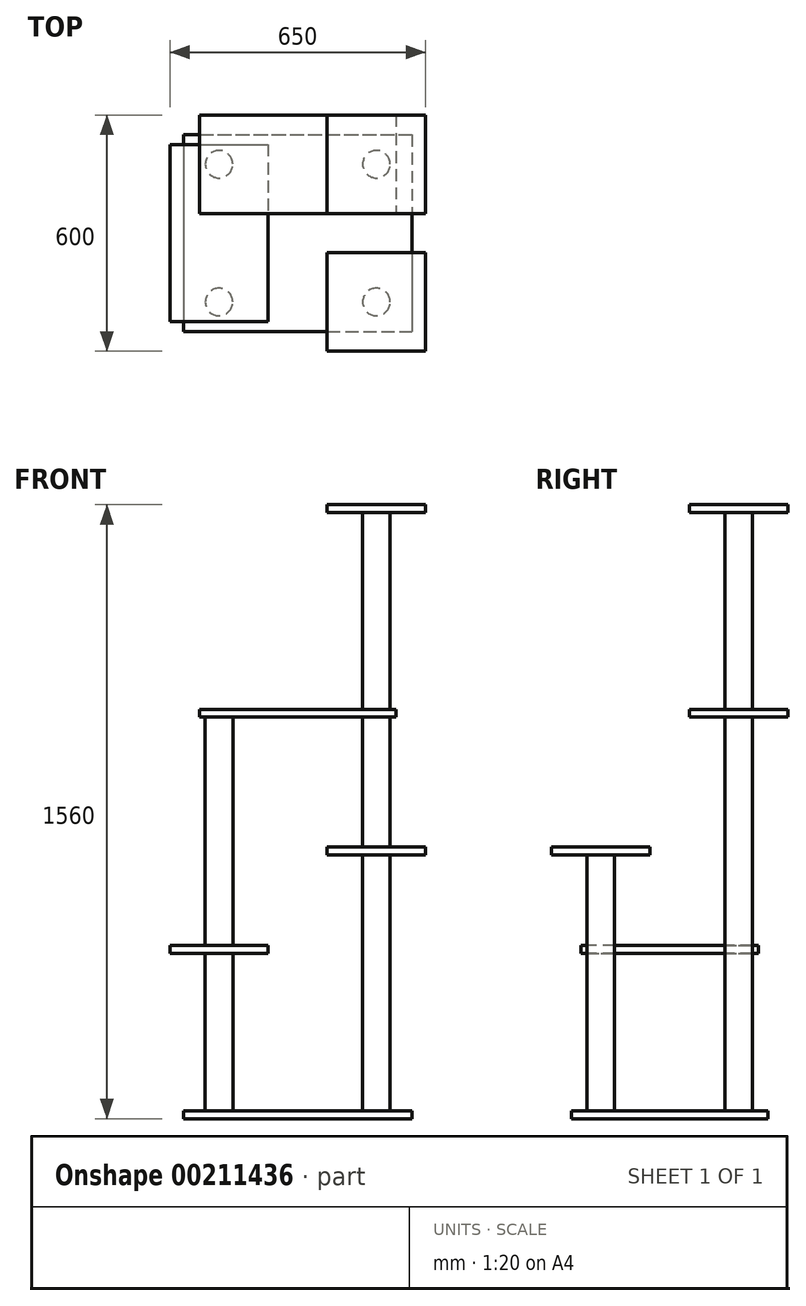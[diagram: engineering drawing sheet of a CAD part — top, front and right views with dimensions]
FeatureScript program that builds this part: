
annotation { "Feature Type Name" : "Feature", "Feature Type Description" : "" }
export const myFeature = defineFeature(function(context is Context, id is Id, definition is map)
    precondition{}
    {
        {
            var Q0;
            Q0=qCreatedBy(makeId("Top.planeOp"),FACE);
            var sketch = newSketch(context, id + "F0", { "sketchPlane" : qUnion([Q0])});
            skLineSegment(sketch, "E0.bottom", {"start": v(-290, 250) * mm, "end": v(290, 250) * mm});
            skLineSegment(sketch, "E0.top", {"start": v(-290, -250) * mm, "end": v(290, -250) * mm});
            skLineSegment(sketch, "E0.left", {"start": v(-290, 250) * mm, "end": v(-290, -250) * mm});
            skLineSegment(sketch, "E0.right", {"start": v(290, 250) * mm, "end": v(290, -250) * mm});
            skPoint(sketch, "E0.middle", {"position": v(0, 0) * mm});
            skSolve(sketch);
        }
        {
            var Q0;
            Q0 = qSketchRegion(id + "F0", true);
            extrude(context, id + "F1", {"entities" : qUnion([Q0]), "depth" : 20 * mm});
        }
        {
            var Q0;
            Q0=makeQuery(id+"F1.opExtrude","CAP_FACE",FACE,{"disambiguationData":[OSD([sQuery(id+"F0.wireOp",EDGE,"E0.bottom"),sQuery(id+"F0.wireOp",EDGE,"E0.top"),sQuery(id+"F0.wireOp",EDGE,"E0.left"),sQuery(id+"F0.wireOp",EDGE,"E0.right")])],"isStart":false});
            var sketch = newSketch(context, id + "F2", { "sketchPlane" : qUnion([Q0])});
            skLineSegment(sketch, "E1.bottom", {"start": v(-200, 175) * mm, "end": v(200, 175) * mm, "construction": true});
            skLineSegment(sketch, "E1.top", {"start": v(-200, -175) * mm, "end": v(200, -175) * mm, "construction": true});
            skLineSegment(sketch, "E1.left", {"start": v(-200, 175) * mm, "end": v(-200, -175) * mm, "construction": true});
            skLineSegment(sketch, "E1.right", {"start": v(200, 175) * mm, "end": v(200, -175) * mm, "construction": true});
            skPoint(sketch, "E1.middle", {"position": v(0, 0) * mm});
            skCircle(sketch, "E2", {"center": v(-200, 175) * mm, "radius": 35 * mm});
            skCircle(sketch, "E3", {"center": v(200, 175) * mm, "radius": 35 * mm});
            skCircle(sketch, "E4", {"center": v(-200, -175) * mm, "radius": 35 * mm});
            skCircle(sketch, "E5", {"center": v(200, -175) * mm, "radius": 35 * mm});
            skSolve(sketch);
        }
        {
            var Q0;
            Q0=makeQuery(id+"F2.imprint","IMPRINT",FACE,{"disambiguationData":[TD([[makeQuery(id+"F2.imprint","IMPRINT",EDGE,{"derivedFrom":sQuery(id+"F2.wireOp",EDGE,"E2")}),1.0]])]});
            var Q1;
            Q1=makeQuery(id+"F2.imprint","IMPRINT",FACE,{"disambiguationData":[TD([[makeQuery(id+"F2.imprint","IMPRINT",EDGE,{"derivedFrom":sQuery(id+"F2.wireOp",EDGE,"E4")}),1.0]])]});
            extrude(context, id + "F3", {"entities" : qUnion([Q0, Q1]), "operationType" : NewBodyOperationType.ADD, "depth" : 400 * mm});
        }
        {
            var Q0;
            Q0=makeQuery(id+"F3.opExtrude","CAP_FACE",FACE,{"disambiguationData":[OSD([sQuery(id+"F2.wireOp",EDGE,"E2")])],"isStart":false});
            var sketch = newSketch(context, id + "F4", { "sketchPlane" : qUnion([Q0])});
            skLineSegment(sketch, "E6.bottom", {"start": v(-325, 225) * mm, "end": v(-75, 225) * mm});
            skLineSegment(sketch, "E6.top", {"start": v(-325, -225) * mm, "end": v(-75, -225) * mm});
            skLineSegment(sketch, "E6.left", {"start": v(-325, 225) * mm, "end": v(-325, -225) * mm});
            skLineSegment(sketch, "E6.right", {"start": v(-75, 225) * mm, "end": v(-75, -225) * mm});
            skPoint(sketch, "E6.middle", {"position": v(-200, 0) * mm});
            skLineSegment(sketch, "E7", {"start": v(-200, 175) * mm, "end": v(-200, -175) * mm, "construction": true});
            skSolve(sketch);
        }
        {
            var Q0;
            Q0 = qSketchRegion(id + "F4", true);
            extrude(context, id + "F5", {"entities" : qUnion([Q0]), "operationType" : NewBodyOperationType.ADD, "depth" : 20 * mm});
        }
        {
            var Q0;
            Q0=makeQuery(id+"F2.imprint","IMPRINT",FACE,{"disambiguationData":[TD([[makeQuery(id+"F2.imprint","IMPRINT",EDGE,{"derivedFrom":sQuery(id+"F2.wireOp",EDGE,"E3")}),1.0]])]});
            extrude(context, id + "F6", {"entities" : qUnion([Q0]), "operationType" : NewBodyOperationType.ADD, "depth" : 1000 * mm});
        }
        {
            var Q0;
            Q0=makeQuery(id+"F5.opExtrude","CAP_FACE",FACE,{"disambiguationData":[OSD([sQuery(id+"F4.wireOp",EDGE,"E6.bottom"),sQuery(id+"F4.wireOp",EDGE,"E6.top"),sQuery(id+"F4.wireOp",EDGE,"E6.left"),sQuery(id+"F4.wireOp",EDGE,"E6.right")])],"isStart":false});
            var sketch = newSketch(context, id + "F7", { "sketchPlane" : qUnion([Q0])});
            skCircle(sketch, "E8.0", {"center": v(-200, 175) * mm, "radius": 35 * mm});
            skSolve(sketch);
        }
        {
            var Q0;
            Q0=makeQuery(id+"F7.imprint","IMPRINT",FACE,{"disambiguationData":[TD([[makeQuery(id+"F7.imprint","IMPRINT",EDGE,{"derivedFrom":sQuery(id+"F7.wireOp",EDGE,"E8.0")}),1.0]])]});
            var Q1;
            Q1=makeQuery(id+"F6.opExtrude","CAP_FACE",FACE,{"disambiguationData":[OSD([sQuery(id+"F2.wireOp",EDGE,"E3")])],"isStart":false});
            extrude(context, id + "F8", {"entities" : qUnion([Q0]), "operationType" : NewBodyOperationType.ADD, "endBound" : BoundingType.UP_TO_SURFACE, "endBoundEntityFace" : qUnion([Q1]), "depth" : 25 * mm});
        }
        {
            var Q0;
            Q0=makeQuery(id+"F2.imprint","IMPRINT",FACE,{"disambiguationData":[TD([[makeQuery(id+"F2.imprint","IMPRINT",EDGE,{"derivedFrom":sQuery(id+"F2.wireOp",EDGE,"E5")}),1.0]])]});
            extrude(context, id + "F9", {"entities" : qUnion([Q0]), "operationType" : NewBodyOperationType.ADD, "depth" : 650 * mm});
        }
        {
            var Q0;
            Q0=makeQuery(id+"F9.opExtrude","CAP_FACE",FACE,{"disambiguationData":[OSD([sQuery(id+"F2.wireOp",EDGE,"E5")])],"isStart":false});
            var sketch = newSketch(context, id + "F10", { "sketchPlane" : qUnion([Q0])});
            skLineSegment(sketch, "E9.bottom", {"start": v(75, -50) * mm, "end": v(325, -50) * mm});
            skLineSegment(sketch, "E9.top", {"start": v(75, -300) * mm, "end": v(325, -300) * mm});
            skLineSegment(sketch, "E9.left", {"start": v(75, -50) * mm, "end": v(75, -300) * mm});
            skLineSegment(sketch, "E9.right", {"start": v(325, -50) * mm, "end": v(325, -300) * mm});
            skPoint(sketch, "E9.middle", {"position": v(200, -175) * mm});
            skSolve(sketch);
        }
        {
            var Q0;
            Q0=makeQuery(id+"F10.imprint","IMPRINT",FACE,{"disambiguationData":[TD([[makeQuery(id+"F10.imprint","IMPRINT",EDGE,{"derivedFrom":sQuery(id+"F10.wireOp",EDGE,"E9.bottom")}),-1.0]])]});
            var Q1;
            Q1=makeQuery(id+"F10.imprint","IMPRINT",FACE,{"disambiguationData":[TD([[makeQuery(id+"F10.imprint","IMPRINT",EDGE,{"derivedFrom":makeQuery(id+"F9.opExtrude","CAP_EDGE",EDGE,{"disambiguationData":[OSD([sQuery(id+"F2.wireOp",EDGE,"E5")])],"isStart":false})}),1.0]])]});
            extrude(context, id + "F11", {"entities" : qUnion([Q0, Q1]), "operationType" : NewBodyOperationType.ADD, "depth" : 20 * mm});
        }
        {
            var Q0;
            Q0=makeQuery(id+"F8.opExtrude","CAP_FACE",FACE,{"disambiguationData":[OSD([sQuery(id+"F7.wireOp",EDGE,"E8.0")])],"isStart":false});
            var sketch = newSketch(context, id + "F12", { "sketchPlane" : qUnion([Q0])});
            skLineSegment(sketch, "E10.bottom", {"start": v(-250, 300) * mm, "end": v(250, 300) * mm});
            skLineSegment(sketch, "E10.top", {"start": v(-250, 50) * mm, "end": v(250, 50) * mm});
            skLineSegment(sketch, "E10.left", {"start": v(-250, 300) * mm, "end": v(-250, 50) * mm});
            skLineSegment(sketch, "E10.right", {"start": v(250, 300) * mm, "end": v(250, 50) * mm});
            skPoint(sketch, "E10.middle", {"position": v(0, 175) * mm});
            skLineSegment(sketch, "E11.0", {"start": v(-200, 175) * mm, "end": v(200, 175) * mm, "construction": true});
            skSolve(sketch);
        }
        {
            var Q0;
            Q0 = qSketchRegion(id + "F12", true);
            extrude(context, id + "F13", {"entities" : qUnion([Q0]), "operationType" : NewBodyOperationType.ADD, "depth" : 20 * mm});
        }
        {
            var Q0;
            Q0=makeQuery(id+"F13.opExtrude","CAP_FACE",FACE,{"disambiguationData":[OSD([sQuery(id+"F12.wireOp",EDGE,"E10.bottom"),sQuery(id+"F12.wireOp",EDGE,"E10.top"),sQuery(id+"F12.wireOp",EDGE,"E10.left"),sQuery(id+"F12.wireOp",EDGE,"E10.right")])],"isStart":false});
            var sketch = newSketch(context, id + "F14", { "sketchPlane" : qUnion([Q0])});
            skCircle(sketch, "E12.0", {"center": v(200, 175) * mm, "radius": 35 * mm});
            skSolve(sketch);
        }
        {
            var Q0;
            Q0 = qSketchRegion(id + "F14", true);
            extrude(context, id + "F15", {"entities" : qUnion([Q0]), "operationType" : NewBodyOperationType.ADD, "depth" : 500 * mm});
        }
        {
            var Q0;
            Q0=makeQuery(id+"F15.opExtrude","CAP_FACE",FACE,{"disambiguationData":[OSD([sQuery(id+"F14.wireOp",EDGE,"E12.0")])],"isStart":false});
            var sketch = newSketch(context, id + "F16", { "sketchPlane" : qUnion([Q0])});
            skLineSegment(sketch, "E13.bottom", {"start": v(75, 300) * mm, "end": v(325, 300) * mm});
            skLineSegment(sketch, "E13.top", {"start": v(75, 50) * mm, "end": v(325, 50) * mm});
            skLineSegment(sketch, "E13.left", {"start": v(75, 300) * mm, "end": v(75, 50) * mm});
            skLineSegment(sketch, "E13.right", {"start": v(325, 300) * mm, "end": v(325, 50) * mm});
            skPoint(sketch, "E13.middle", {"position": v(200, 175) * mm});
            skSolve(sketch);
        }
        {
            var Q0;
            Q0 = qSketchRegion(id + "F16", true);
            extrude(context, id + "F17", {"entities" : qUnion([Q0]), "operationType" : NewBodyOperationType.ADD, "depth" : 20 * mm});
        }
    });
